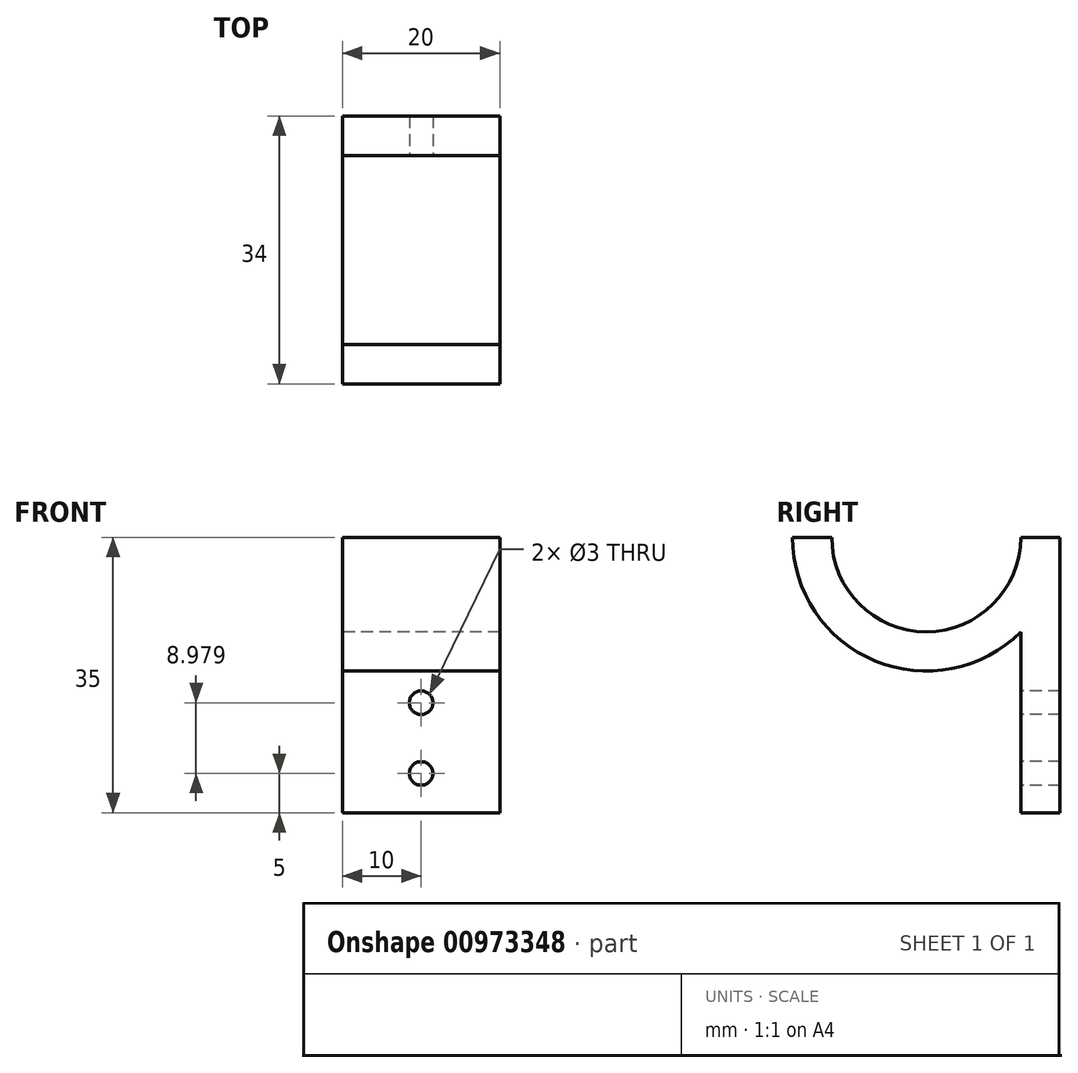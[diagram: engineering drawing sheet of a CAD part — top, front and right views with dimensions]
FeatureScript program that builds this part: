
annotation { "Feature Type Name" : "Feature", "Feature Type Description" : "" }
export const myFeature = defineFeature(function(context is Context, id is Id, definition is map)
    precondition{}
    {
        {
            var Q0;
            Q0=qCreatedBy(makeId("Right.planeOp"),FACE);
            var sketch = newSketch(context, id + "F0", { "sketchPlane" : qUnion([Q0])});
            skArc(sketch, "E0", {"start": v(-12, 0) * mm, "mid": v(0, -12) * mm, "end": v(12, 0) * mm});
            skLineSegment(sketch, "E1", {"start": v(-12, 0) * mm, "end": v(12, 0) * mm});
            skPoint(sketch, "E2", {"position": v(-12, 0) * mm});
            skPoint(sketch, "E3", {"position": v(12, 0) * mm});
            skArc(sketch, "E4.0", {"start": v(-17, 0) * mm, "mid": v(0, -17) * mm, "end": v(17, 0) * mm});
            skLineSegment(sketch, "E5", {"start": v(-12, 0) * mm, "end": v(-17, 0) * mm});
            skLineSegment(sketch, "E6", {"start": v(12, 0) * mm, "end": v(17, 0) * mm});
            skLineSegment(sketch, "E7.top", {"start": v(12, -30) * mm, "end": v(17, -30) * mm});
            skLineSegment(sketch, "E7.left", {"start": v(12, 0) * mm, "end": v(12, -30) * mm});
            skLineSegment(sketch, "E7.right", {"start": v(17, 0) * mm, "end": v(17, -30) * mm});
            skSolve(sketch);
        }
        {
            var Q0;
            {var subQ0=sQuery(id+"F0.wireOp",EDGE,"E0");Q0=makeQuery(id+"F0.imprint","IMPRINT",FACE,{"disambiguationData":[TD([[makeQuery(id+"F0.imprint","IMPRINT",EDGE,{"derivedFrom":subQ0}),-1.0]])]});}
            var Q1;
            {var subQ4=sQuery(id+"F0.wireOp",EDGE,"E7.top");Q1=makeQuery(id+"F0.imprint","IMPRINT",FACE,{"disambiguationData":[TD([[makeQuery(id+"F0.imprint","IMPRINT",EDGE,{"derivedFrom":subQ4}),1.0]])]});}
            var Q2;
            {var subQ3=sQuery(id+"F0.wireOp",EDGE,"E6");Q2=makeQuery(id+"F0.imprint","IMPRINT",FACE,{"disambiguationData":[TD([[makeQuery(id+"F0.imprint","IMPRINT",EDGE,{"derivedFrom":subQ3}),-1.0]])]});}
            var Q3;
            {var subQ0=sQuery(id+"F0.wireOp",EDGE,"E0");Q3=makeQuery(id+"F0.imprint","IMPRINT",FACE,{"disambiguationData":[TD([[makeQuery(id+"F0.imprint","IMPRINT",EDGE,{"derivedFrom":subQ0}),-1.0]])]});}
            extrude(context, id + "F1", {"entities" : qUnion([Q0, Q1, Q2, Q3]), "depth" : 20 * mm, "offsetDistance" : 25 * mm, "symmetric" : true});
        }
        {
            var Q0;
            Q0=makeQuery(id+"F1.opExtrude","SWEPT_FACE",FACE,{"disambiguationData":[OSD([sQuery(id+"F0.wireOp",EDGE,"E7.left")])]});
            var sketch = newSketch(context, id + "F2", { "sketchPlane" : qUnion([Q0])});
            skLineSegment(sketch, "E8", {"start": v(0, -30) * mm, "end": v(0, -12.04) * mm});
            skLineSegment(sketch, "E9", {"start": v(0, -12.04) * mm, "end": v(0, -21.02) * mm});
            skSolve(sketch);
        }
        {
            var Q0;
            Q0=makeQuery(id+"F1.opExtrude","SWEPT_FACE",FACE,{"disambiguationData":[OSD([sQuery(id+"F0.wireOp",EDGE,"E7.top")])]});
            extrude(context, id + "F3", {"entities" : qUnion([Q0]), "operationType" : NewBodyOperationType.ADD, "depth" : 5 * mm, "offsetDistance" : 25 * mm});
        }
        {
            var Q0;
            Q0=sQuery(id+"F2.wireOp",VERTEX,"E8.start");
            var Q1;
            Q1=sQuery(id+"F2.wireOp",VERTEX,"E9.end");
            var Q2;
            Q2=makeQuery(id+"F1.opExtrude","SWEPT_BODY",BODY,{"disambiguationData":[OSD([sQuery(id+"F0.wireOp",EDGE,"E0"),sQuery(id+"F0.wireOp",EDGE,"E4.0"),sQuery(id+"F0.wireOp",EDGE,"E5"),sQuery(id+"F0.wireOp",EDGE,"E6"),sQuery(id+"F0.wireOp",EDGE,"E7.top"),sQuery(id+"F0.wireOp",EDGE,"E7.left"),sQuery(id+"F0.wireOp",EDGE,"E7.right")])]});
            hole(context, id + "F4", {"style" : HoleStyle.SIMPLE, "endStyle" : HoleEndStyle.THROUGH, "holeDiameter" : 3 * mm, "majorDiameter" : 5 * mm, "isTappedThrough" : true, "tappedDepth" : 12 * mm, "tapClearance" : 3, "locations" : qUnion([Q0, Q1]), "scope" : qUnion([Q2])});
        }
    });
